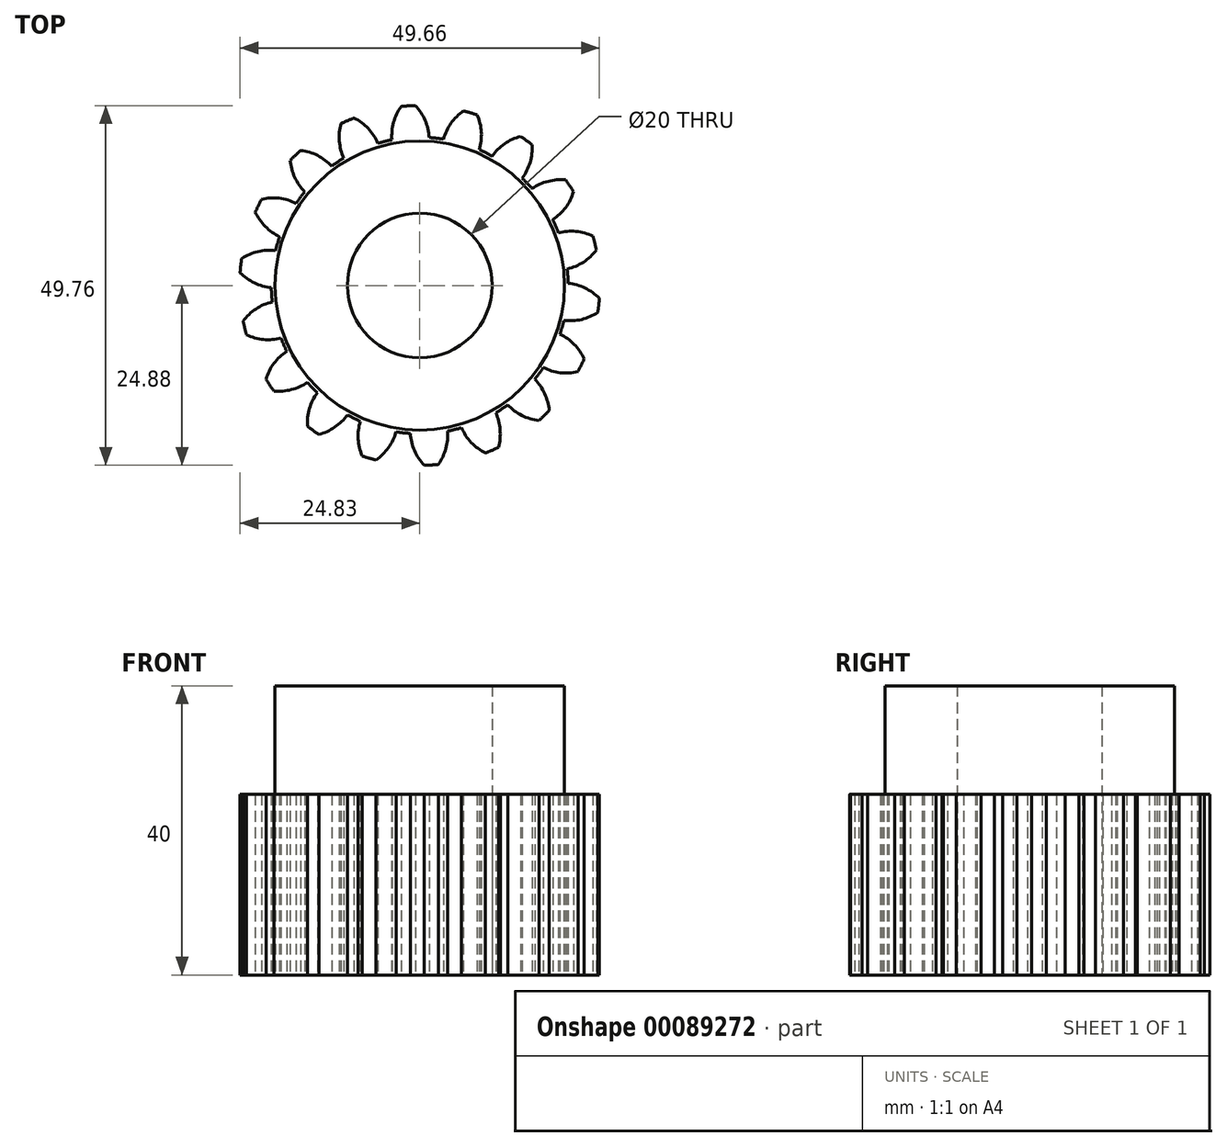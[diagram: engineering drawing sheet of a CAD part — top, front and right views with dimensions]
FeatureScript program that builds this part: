
annotation { "Feature Type Name" : "Feature", "Feature Type Description" : "" }
export const myFeature = defineFeature(function(context is Context, id is Id, definition is map)
    precondition{}
    {
        {
            var Q0;
            Q0=qCreatedBy(makeId("Top.planeOp"),FACE);
            var sketch = newSketch(context, id + "F0", { "sketchPlane" : qUnion([Q0])});
            skCircle(sketch, "E0", {"center": v(0, 0) * mm, "radius": 25.4 * mm, "construction": true});
            skCircle(sketch, "E1", {"center": v(0, 0) * mm, "radius": 24.9 * mm});
            skCircle(sketch, "E2", {"center": v(0, 0) * mm, "radius": 22.13 * mm, "construction": true});
            skCircle(sketch, "E3", {"center": v(0, 0) * mm, "radius": 20.9 * mm, "construction": true});
            skLineSegment(sketch, "E4", {"start": v(0, 20.9) * mm, "end": v(0, 25.4) * mm, "construction": true});
            skLineSegment(sketch, "E5", {"start": v(-6.36, 24.6) * mm, "end": v(-5.23, 20.23) * mm, "construction": true});
            skLineSegment(sketch, "E6", {"start": v(-5.23, 20.23) * mm, "end": v(0, 22.13) * mm, "construction": true});
            skLineSegment(sketch, "E7", {"start": v(-13.83, 20.7) * mm, "end": v(-14.11, 21.12) * mm});
            skLineSegment(sketch, "E8", {"start": v(0, 22.13) * mm, "end": v(6.63, 24.52) * mm, "construction": true});
            skLineSegment(sketch, "E9", {"start": v(10.24, 18.22) * mm, "end": v(3.9, 21.78) * mm, "construction": true});
            skCircle(sketch, "E10", {"center": v(10.24, 18.22) * mm, "radius": 7.26 * mm});
            skLineSegment(sketch, "E11", {"start": v(3.9, 21.78) * mm, "end": v(4.4, 24.5) * mm, "construction": true});
            skLineSegment(sketch, "E12", {"start": v(15.28, 19.65) * mm, "end": v(13.58, 17.47) * mm, "construction": true});
            skLineSegment(sketch, "E13", {"start": v(10.13, 22.74) * mm, "end": v(9, 20.21) * mm, "construction": true});
            skLineSegment(sketch, "E14", {"start": v(3.9, 21.78) * mm, "end": v(10.13, 22.74) * mm, "construction": true});
            skLineSegment(sketch, "E15", {"start": v(13.58, 17.47) * mm, "end": v(10.13, 22.74) * mm, "construction": true});
            skCircle(sketch, "E16", {"center": v(0, 0) * mm, "radius": 20.5 * mm});
            skLineSegment(sketch, "E17", {"start": v(5.68, 19.55) * mm, "end": v(3.26, 20.25) * mm, "construction": true});
            skLineSegment(sketch, "E18", {"start": v(9, 20.21) * mm, "end": v(8.5, 20.25) * mm});
            skLineSegment(sketch, "E19", {"start": v(8.5, 20.25) * mm, "end": v(1.77, 20.83) * mm, "construction": true});
            skCircle(sketch, "E20", {"center": v(1.77, 20.83) * mm, "radius": 6.75 * mm});
            skLineSegment(sketch, "E21", {"start": v(5.68, 19.55) * mm, "end": v(7.21, 24.82) * mm, "construction": true});
            skLineSegment(sketch, "E22", {"start": v(9, 20.21) * mm, "end": v(3.9, 21.78) * mm, "construction": true});
            skCircle(sketch, "E23", {"center": v(0, 0) * mm, "radius": 10 * mm});
            skSolve(sketch);
        }
        {
            var Q0;
            {var subQ0=sQuery(id+"F0.wireOp",EDGE,"E20");var subQ3=sQuery(id+"F0.wireOp",EDGE,"E10");var subQ4=makeQuery(id+"F0.imprint","INTERSECT",VERTEX,{"disambiguationData":[OD(1.0)],"derivedFrom":[subQ3,subQ0]});Q0=makeQuery(id+"F0.imprint","IMPRINT",FACE,{"disambiguationData":[TD([[makeQuery(id+"F0.imprint","IMPRINT",EDGE,{"disambiguationData":[TD([[subQ4,-1.0]])],"derivedFrom":subQ3}),-1.0]])]});}
            var Q1;
            {var subQ0=sQuery(id+"F0.wireOp",EDGE,"E20");var subQ3=sQuery(id+"F0.wireOp",EDGE,"E10");var subQ4=makeQuery(id+"F0.imprint","INTERSECT",VERTEX,{"disambiguationData":[OD(1.0)],"derivedFrom":[subQ3,subQ0]});Q1=makeQuery(id+"F0.imprint","IMPRINT",FACE,{"disambiguationData":[TD([[makeQuery(id+"F0.imprint","IMPRINT",EDGE,{"disambiguationData":[TD([[subQ4,-1.0]])],"derivedFrom":subQ3}),1.0]])]});}
            var Q2;
            {var subQ1=sQuery(id+"F0.wireOp",EDGE,"E16");var subQ3=sQuery(id+"F0.wireOp",EDGE,"E10");var subQ5=makeQuery(id+"F0.imprint","INTERSECT",VERTEX,{"disambiguationData":[OD(0.0)],"derivedFrom":[subQ3,subQ1]});Q2=makeQuery(id+"F0.imprint","IMPRINT",FACE,{"disambiguationData":[TD([[makeQuery(id+"F0.imprint","IMPRINT",EDGE,{"disambiguationData":[TD([[subQ5,-1.0]])],"derivedFrom":subQ3}),1.0]])]});}
            var Q3;
            {var subQ1=sQuery(id+"F0.wireOp",EDGE,"E16");var subQ3=sQuery(id+"F0.wireOp",EDGE,"E10");var subQ5=makeQuery(id+"F0.imprint","INTERSECT",VERTEX,{"disambiguationData":[OD(0.0)],"derivedFrom":[subQ3,subQ1]});Q3=makeQuery(id+"F0.imprint","IMPRINT",FACE,{"disambiguationData":[TD([[makeQuery(id+"F0.imprint","IMPRINT",EDGE,{"disambiguationData":[TD([[subQ5,-1.0]])],"derivedFrom":subQ3}),-1.0]])]});}
            var Q4;
            {var subQ0=sQuery(id+"F0.wireOp",EDGE,"E20");var subQ3=makeQuery(id+"F0.imprint","IMPRINT",VERTEX,{"derivedFrom":subQ0});Q4=makeQuery(id+"F0.imprint","IMPRINT",FACE,{"disambiguationData":[TD([[makeQuery(id+"F0.imprint","IMPRINT",EDGE,{"disambiguationData":[TD([[subQ3,-1.0]])],"derivedFrom":subQ0}),1.0]])]});}
            extrude(context, id + "F1", {"entities" : qUnion([Q0, Q1, Q2, Q3, Q4]), "depth" : 25 * mm});
        }
        {
            var Q0;
            Q0=makeQuery(id+"F1.opExtrude","SWEPT_BODY",BODY,{"disambiguationData":[OSD([sQuery(id+"F0.wireOp",EDGE,"E1"),sQuery(id+"F0.wireOp",EDGE,"E10"),sQuery(id+"F0.wireOp",EDGE,"E16"),sQuery(id+"F0.wireOp",EDGE,"E20")])]});
            var Q1;
            Q1=makeQuery(id+"F1.opExtrude","CAP_EDGE",EDGE,{"disambiguationData":[OSD([sQuery(id+"F0.wireOp",EDGE,"E16")])],"isStart":false});
            circularPattern(context, id + "F2", {"operationType" : NewBodyOperationType.ADD, "entities" : qUnion([Q0]), "axis" : qUnion([Q1]), "angle" : 360 * degree, "instanceCount" : 18, "equalSpace" : true});
        }
        {
            var Q0;
            {var subQ0=makeQuery(id+"F1.opExtrude","CAP_FACE",FACE,{"disambiguationData":[OSD([sQuery(id+"F0.wireOp",EDGE,"E1"),sQuery(id+"F0.wireOp",EDGE,"E10"),sQuery(id+"F0.wireOp",EDGE,"E16"),sQuery(id+"F0.wireOp",EDGE,"E20"),sQuery(id+"F0.wireOp",EDGE,"E23")])],"isStart":false});Q0=makeQuery(id+"F2.boolean.opBoolean","MERGE",FACE,{"derivedFrom":[subQ0,makeQuery(id+"F2.opPattern","COPY",FACE,{"derivedFrom":subQ0,"instanceName":"1"}),makeQuery(id+"F2.opPattern","COPY",FACE,{"derivedFrom":subQ0,"instanceName":"2"}),makeQuery(id+"F2.opPattern","COPY",FACE,{"derivedFrom":subQ0,"instanceName":"3"}),makeQuery(id+"F2.opPattern","COPY",FACE,{"derivedFrom":subQ0,"instanceName":"4"}),makeQuery(id+"F2.opPattern","COPY",FACE,{"derivedFrom":subQ0,"instanceName":"5"}),makeQuery(id+"F2.opPattern","COPY",FACE,{"derivedFrom":subQ0,"instanceName":"6"}),makeQuery(id+"F2.opPattern","COPY",FACE,{"derivedFrom":subQ0,"instanceName":"7"}),makeQuery(id+"F2.opPattern","COPY",FACE,{"derivedFrom":subQ0,"instanceName":"8"}),makeQuery(id+"F2.opPattern","COPY",FACE,{"derivedFrom":subQ0,"instanceName":"9"}),makeQuery(id+"F2.opPattern","COPY",FACE,{"derivedFrom":subQ0,"instanceName":"10"}),makeQuery(id+"F2.opPattern","COPY",FACE,{"derivedFrom":subQ0,"instanceName":"11"}),makeQuery(id+"F2.opPattern","COPY",FACE,{"derivedFrom":subQ0,"instanceName":"12"}),makeQuery(id+"F2.opPattern","COPY",FACE,{"derivedFrom":subQ0,"instanceName":"13"}),makeQuery(id+"F2.opPattern","COPY",FACE,{"derivedFrom":subQ0,"instanceName":"14"}),makeQuery(id+"F2.opPattern","COPY",FACE,{"derivedFrom":subQ0,"instanceName":"15"}),makeQuery(id+"F2.opPattern","COPY",FACE,{"derivedFrom":subQ0,"instanceName":"16"}),makeQuery(id+"F2.opPattern","COPY",FACE,{"derivedFrom":subQ0,"instanceName":"17"})]});}
            var sketch = newSketch(context, id + "F3", { "sketchPlane" : qUnion([Q0])});
            skCircle(sketch, "E24", {"center": v(0, 0) * mm, "radius": 20 * mm});
            skSolve(sketch);
        }
        {
            var Q0;
            Q0=makeQuery(id+"F3.imprint","IMPRINT",FACE,{"disambiguationData":[TD([[makeQuery(id+"F3.imprint","IMPRINT",EDGE,{"derivedFrom":sQuery(id+"F3.wireOp",EDGE,"E24")}),1.0]])]});
            extrude(context, id + "F4", {"entities" : qUnion([Q0]), "operationType" : NewBodyOperationType.ADD, "depth" : 15 * mm});
        }
    });
